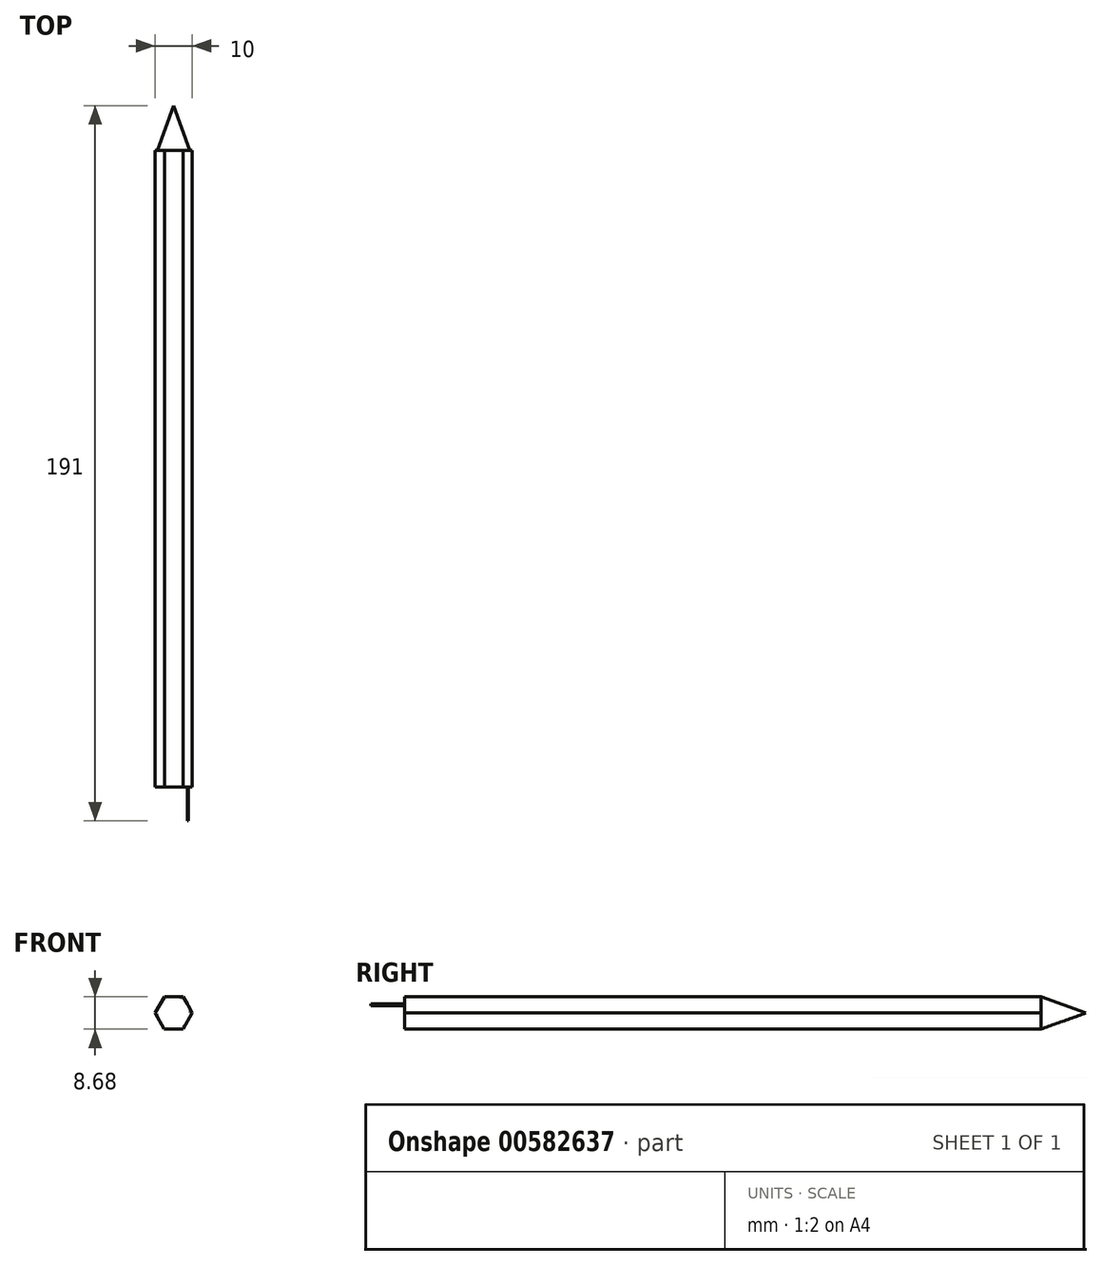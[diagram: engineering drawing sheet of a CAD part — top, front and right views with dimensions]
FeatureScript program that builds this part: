
annotation { "Feature Type Name" : "Feature", "Feature Type Description" : "" }
export const myFeature = defineFeature(function(context is Context, id is Id, definition is map)
    precondition{}
    {
        {
            var Q0;
            Q0=qCreatedBy(makeId("Front.planeOp"),FACE);
            var sketch = newSketch(context, id + "F0", { "sketchPlane" : qUnion([Q0])});
            skCircle(sketch, "E0.cCircle", {"center": v(0, 0) * mm, "radius": 4.33 * mm, "construction": true});
            skLineSegment(sketch, "E0.0", {"start": v(2.51, 4.32) * mm, "end": v(5, -0.02) * mm});
            skLineSegment(sketch, "E0.1", {"start": v(5, -0.02) * mm, "end": v(2.49, -4.34) * mm});
            skLineSegment(sketch, "E0.2", {"start": v(2.49, -4.34) * mm, "end": v(-2.51, -4.32) * mm});
            skLineSegment(sketch, "E0.3", {"start": v(-2.51, -4.32) * mm, "end": v(-5, 0.02) * mm});
            skLineSegment(sketch, "E0.4", {"start": v(-5, 0.02) * mm, "end": v(-2.49, 4.34) * mm});
            skLineSegment(sketch, "E0.5", {"start": v(-2.49, 4.34) * mm, "end": v(2.51, 4.32) * mm});
            skPoint(sketch, "E0.0.midPoint", {"position": v(3.76, 2.15) * mm});
            skSolve(sketch);
        }
        {
            var Q0;
            Q0 = qSketchRegion(id + "F0", true);
            extrude(context, id + "F1", {"entities" : qUnion([Q0]), "depth" : 170 * mm, "offsetDistance" : 25 * mm});
        }
        {
            var Q0;
            Q0=qCreatedBy(makeId("Top.planeOp"),FACE);
            var sketch = newSketch(context, id + "F2", { "sketchPlane" : qUnion([Q0])});
            skLineSegment(sketch, "E1", {"start": v(0, 0) * mm, "end": v(0, 12) * mm});
            skLineSegment(sketch, "E2", {"start": v(0, 0) * mm, "end": v(-4.33, 0) * mm});
            skLineSegment(sketch, "E3", {"start": v(-4.33, 0) * mm, "end": v(0, 12) * mm});
            skSolve(sketch);
        }
        {
            var Q0;
            Q0=makeQuery(id+"F2.imprint","IMPRINT",FACE,{"disambiguationData":[TD([[makeQuery(id+"F2.imprint","IMPRINT",EDGE,{"derivedFrom":sQuery(id+"F2.wireOp",EDGE,"E1")}),1.0]])]});
            var Q1;
            Q1=sQuery(id+"F2.wireOp",EDGE,"E1");
            revolve(context, id + "F3", {"operationType" : NewBodyOperationType.ADD, "entities" : qUnion([Q0]), "axis" : qUnion([Q1]), "revolveType" : RevolveType.FULL});
        }
        {
            var Q0;
            Q0=makeQuery(id+"F1.opExtrude","CAP_FACE",FACE,{"disambiguationData":[OSD([sQuery(id+"F0.wireOp",EDGE,"E0.0"),sQuery(id+"F0.wireOp",EDGE,"E0.1"),sQuery(id+"F0.wireOp",EDGE,"E0.2"),sQuery(id+"F0.wireOp",EDGE,"E0.3"),sQuery(id+"F0.wireOp",EDGE,"E0.4"),sQuery(id+"F0.wireOp",EDGE,"E0.5")])],"isStart":false});
            var sketch = newSketch(context, id + "F4", { "sketchPlane" : qUnion([Q0])});
            skCircle(sketch, "E4", {"center": v(0, 0) * mm, "radius": 4.34 * mm});
            skSolve(sketch);
        }
        {
            var Q0;
            {var subQ0=sQuery(id+"F4.wireOp",EDGE,"E4");var subQ4=makeQuery(id+"F1.opExtrude","CAP_EDGE",EDGE,{"disambiguationData":[OSD([sQuery(id+"F0.wireOp",EDGE,"E0.0")])],"isStart":false});var subQ12=makeQuery(id+"F4.imprint","INTERSECT",VERTEX,{"disambiguationData":[OD(0.0)],"derivedFrom":[subQ4,subQ0]});Q0=makeQuery(id+"F4.imprint","IMPRINT",FACE,{"disambiguationData":[TD([[makeQuery(id+"F4.imprint","IMPRINT",EDGE,{"disambiguationData":[TD([[subQ12,-1.0]])],"derivedFrom":subQ0}),1.0]])]});}
            extrude(context, id + "F5", {"entities" : qUnion([Q0]), "operationType" : NewBodyOperationType.ADD, "depth" : 9 * mm, "offsetDistance" : 25 * mm});
        }
    });
